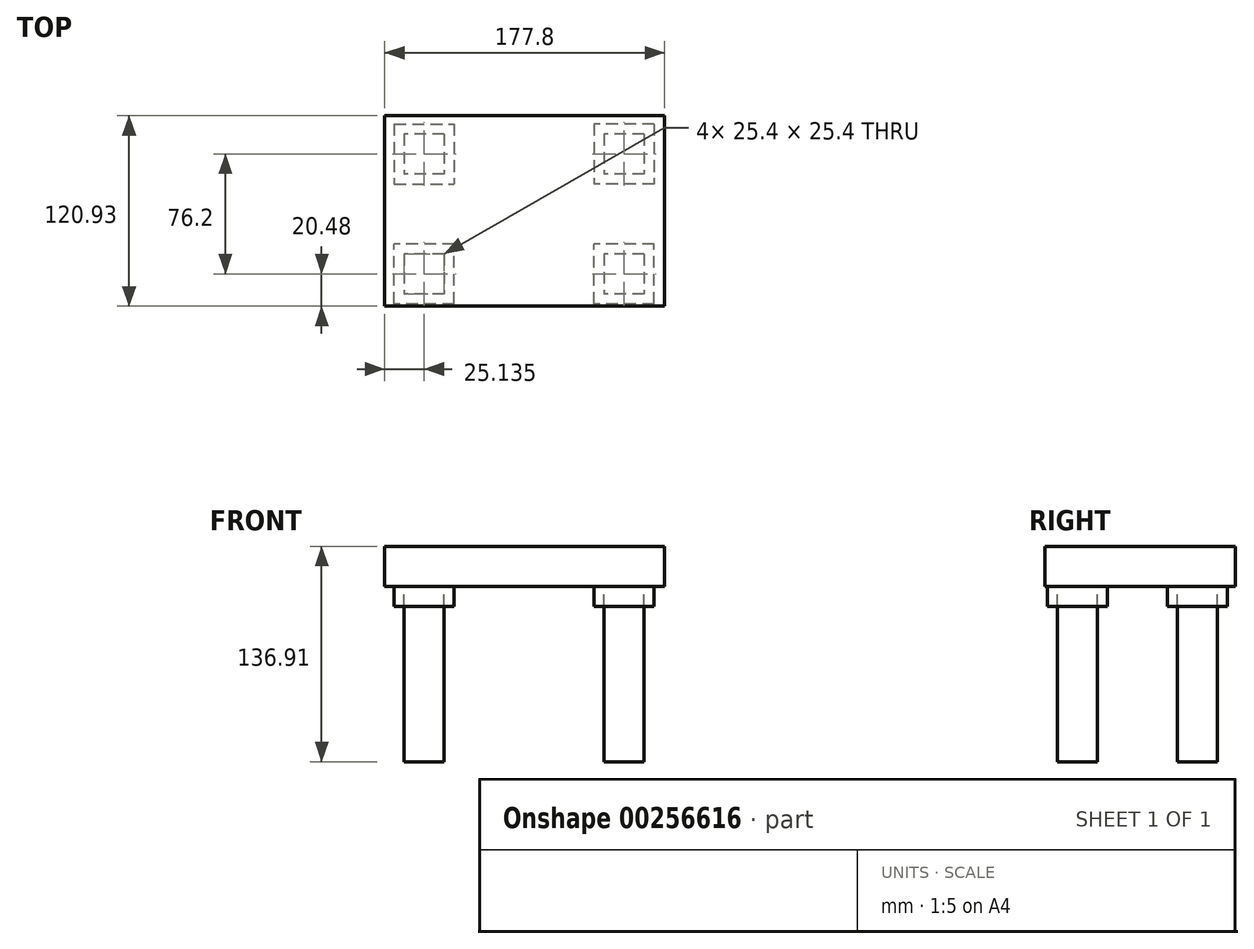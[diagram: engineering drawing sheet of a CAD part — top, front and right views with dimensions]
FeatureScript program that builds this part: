
annotation { "Feature Type Name" : "Feature", "Feature Type Description" : "" }
export const myFeature = defineFeature(function(context is Context, id is Id, definition is map)
    precondition{}
    {
        {
            var Q0;
            Q0=qCreatedBy(makeId("Top.planeOp"),FACE);
            var sketch = newSketch(context, id + "F0", { "sketchPlane" : qUnion([Q0])});
            skLineSegment(sketch, "E0.bottom", {"start": v(-24.92, 50.96) * mm, "end": v(-50.32, 50.96) * mm});
            skLineSegment(sketch, "E0.top", {"start": v(-24.92, 25.56) * mm, "end": v(-50.32, 25.56) * mm});
            skLineSegment(sketch, "E0.left", {"start": v(-24.92, 50.96) * mm, "end": v(-24.92, 25.56) * mm});
            skLineSegment(sketch, "E0.right", {"start": v(-50.32, 50.96) * mm, "end": v(-50.32, 25.56) * mm});
            skPoint(sketch, "E0.middle", {"position": v(-37.62, 38.26) * mm});
            skLineSegment(sketch, "E1", {"start": v(-37.62, 38.26) * mm, "end": v(89.38, 38.26) * mm});
            skLineSegment(sketch, "E2.bottom", {"start": v(102.08, 50.96) * mm, "end": v(76.68, 50.96) * mm});
            skLineSegment(sketch, "E2.top", {"start": v(102.08, 25.56) * mm, "end": v(76.68, 25.56) * mm});
            skLineSegment(sketch, "E2.left", {"start": v(102.08, 50.96) * mm, "end": v(102.08, 25.56) * mm});
            skLineSegment(sketch, "E2.right", {"start": v(76.68, 50.96) * mm, "end": v(76.68, 25.56) * mm});
            skPoint(sketch, "E2.middle", {"position": v(89.38, 38.26) * mm});
            skLineSegment(sketch, "E3", {"start": v(-37.62, 38.26) * mm, "end": v(-37.62, -37.94) * mm});
            skLineSegment(sketch, "E4.bottom", {"start": v(-24.92, -25.24) * mm, "end": v(-50.32, -25.24) * mm});
            skLineSegment(sketch, "E4.top", {"start": v(-24.92, -50.64) * mm, "end": v(-50.32, -50.64) * mm});
            skLineSegment(sketch, "E4.left", {"start": v(-24.92, -25.24) * mm, "end": v(-24.92, -50.64) * mm});
            skLineSegment(sketch, "E4.right", {"start": v(-50.32, -25.24) * mm, "end": v(-50.32, -50.64) * mm});
            skPoint(sketch, "E4.middle", {"position": v(-37.62, -37.94) * mm});
            skLineSegment(sketch, "E5", {"start": v(-37.62, -37.94) * mm, "end": v(89.38, -37.94) * mm});
            skLineSegment(sketch, "E6.bottom", {"start": v(102.08, -25.24) * mm, "end": v(76.68, -25.24) * mm});
            skLineSegment(sketch, "E6.top", {"start": v(102.08, -50.64) * mm, "end": v(76.68, -50.64) * mm});
            skLineSegment(sketch, "E6.left", {"start": v(102.08, -25.24) * mm, "end": v(102.08, -50.64) * mm});
            skLineSegment(sketch, "E6.right", {"start": v(76.68, -25.24) * mm, "end": v(76.68, -50.64) * mm});
            skPoint(sketch, "E6.middle", {"position": v(89.38, -37.94) * mm});
            skLineSegment(sketch, "E7", {"start": v(89.38, 38.26) * mm, "end": v(89.38, -37.94) * mm});
            skLineSegment(sketch, "E8.bottom", {"start": v(-18.57, -56.99) * mm, "end": v(-56.67, -56.99) * mm});
            skLineSegment(sketch, "E8.top", {"start": v(-18.57, -18.89) * mm, "end": v(-56.67, -18.89) * mm});
            skLineSegment(sketch, "E8.left", {"start": v(-18.57, -56.99) * mm, "end": v(-18.57, -18.89) * mm});
            skLineSegment(sketch, "E8.right", {"start": v(-56.67, -56.99) * mm, "end": v(-56.67, -18.89) * mm});
            skLineSegment(sketch, "E9.bottom", {"start": v(108.43, -56.99) * mm, "end": v(70.33, -56.99) * mm});
            skLineSegment(sketch, "E9.top", {"start": v(108.43, -18.89) * mm, "end": v(70.33, -18.89) * mm});
            skLineSegment(sketch, "E9.left", {"start": v(108.43, -56.99) * mm, "end": v(108.43, -18.89) * mm});
            skLineSegment(sketch, "E9.right", {"start": v(70.33, -56.99) * mm, "end": v(70.33, -18.89) * mm});
            skLineSegment(sketch, "E10.bottom", {"start": v(108.43, 57.31) * mm, "end": v(70.33, 57.31) * mm});
            skLineSegment(sketch, "E10.top", {"start": v(108.43, 19.21) * mm, "end": v(70.33, 19.21) * mm});
            skLineSegment(sketch, "E10.left", {"start": v(108.43, 57.31) * mm, "end": v(108.43, 19.21) * mm});
            skLineSegment(sketch, "E10.right", {"start": v(70.33, 57.31) * mm, "end": v(70.33, 19.21) * mm});
            skLineSegment(sketch, "E11.bottom", {"start": v(-56.67, 57.31) * mm, "end": v(-18.57, 57.31) * mm});
            skLineSegment(sketch, "E11.top", {"start": v(-56.67, 19.21) * mm, "end": v(-18.57, 19.21) * mm});
            skLineSegment(sketch, "E11.left", {"start": v(-56.67, 57.31) * mm, "end": v(-56.67, 19.21) * mm});
            skLineSegment(sketch, "E11.right", {"start": v(-18.57, 57.31) * mm, "end": v(-18.57, 19.21) * mm});
            skSolve(sketch);
        }
        {
            var Q0;
            {var subQ4=sQuery(id+"F0.wireOp",EDGE,"E2.bottom");Q0=makeQuery(id+"F0.imprint","IMPRINT",FACE,{"disambiguationData":[TD([[makeQuery(id+"F0.imprint","IMPRINT",EDGE,{"derivedFrom":subQ4}),1.0]])]});}
            var Q1;
            {var subQ1=sQuery(id+"F0.wireOp",EDGE,"E4.top");Q1=makeQuery(id+"F0.imprint","IMPRINT",FACE,{"disambiguationData":[TD([[makeQuery(id+"F0.imprint","IMPRINT",EDGE,{"derivedFrom":subQ1}),-1.0]])]});}
            var Q2;
            {var subQ1=sQuery(id+"F0.wireOp",EDGE,"E6.top");Q2=makeQuery(id+"F0.imprint","IMPRINT",FACE,{"disambiguationData":[TD([[makeQuery(id+"F0.imprint","IMPRINT",EDGE,{"derivedFrom":subQ1}),-1.0]])]});}
            var Q3;
            {var subQ0=sQuery(id+"F0.wireOp",EDGE,"E0.left");var subQ1=sQuery(id+"F0.wireOp",EDGE,"E0.top");var subQ2=makeQuery(id+"F0.imprint","INTERSECT",VERTEX,{"derivedFrom":[subQ1,subQ0]});Q3=makeQuery(id+"F0.imprint","IMPRINT",FACE,{"disambiguationData":[TD([[makeQuery(id+"F0.imprint","IMPRINT",EDGE,{"disambiguationData":[TD([[subQ2,-1.0]])],"derivedFrom":subQ1}),-1.0]])]});}
            var Q4;
            {var subQ0=sQuery(id+"F0.wireOp",EDGE,"E7");var subQ1=sQuery(id+"F0.wireOp",EDGE,"E1");var subQ2=makeQuery(id+"F0.imprint","INTERSECT",VERTEX,{"derivedFrom":[subQ1,subQ0]});Q4=makeQuery(id+"F0.imprint","IMPRINT",FACE,{"disambiguationData":[TD([[makeQuery(id+"F0.imprint","IMPRINT",EDGE,{"disambiguationData":[TD([[subQ2,1.0]])],"derivedFrom":subQ1}),-1.0]])]});}
            var Q5;
            {var subQ0=sQuery(id+"F0.wireOp",EDGE,"E5");var subQ1=sQuery(id+"F0.wireOp",EDGE,"E3");var subQ2=makeQuery(id+"F0.imprint","INTERSECT",VERTEX,{"derivedFrom":[subQ1,subQ0]});Q5=makeQuery(id+"F0.imprint","IMPRINT",FACE,{"disambiguationData":[TD([[makeQuery(id+"F0.imprint","IMPRINT",EDGE,{"disambiguationData":[TD([[subQ2,1.0]])],"derivedFrom":subQ1}),1.0]])]});}
            var Q6;
            {var subQ0=sQuery(id+"F0.wireOp",EDGE,"E7");var subQ1=sQuery(id+"F0.wireOp",EDGE,"E5");var subQ2=makeQuery(id+"F0.imprint","INTERSECT",VERTEX,{"derivedFrom":[subQ1,subQ0]});Q6=makeQuery(id+"F0.imprint","IMPRINT",FACE,{"disambiguationData":[TD([[makeQuery(id+"F0.imprint","IMPRINT",EDGE,{"disambiguationData":[TD([[subQ2,1.0]])],"derivedFrom":subQ1}),1.0]])]});}
            var Q7;
            {var subQ2=sQuery(id+"F0.wireOp",EDGE,"E0.bottom");Q7=makeQuery(id+"F0.imprint","IMPRINT",FACE,{"disambiguationData":[TD([[makeQuery(id+"F0.imprint","IMPRINT",EDGE,{"derivedFrom":subQ2}),1.0]])]});}
            extrude(context, id + "F1", {"entities" : qUnion([Q0, Q1, Q2, Q3, Q4, Q5, Q6, Q7]), "oppositeDirection" : true, "depth" : 111.5 * mm});
        }
        {
            var Q0;
            Q0=qCreatedBy(makeId("Top.planeOp"),FACE);
            var sketch = newSketch(context, id + "F2", { "sketchPlane" : qUnion([Q0])});
            skLineSegment(sketch, "E12.bottom", {"start": v(-62.75, 62.51) * mm, "end": v(115.05, 62.51) * mm});
            skLineSegment(sketch, "E12.top", {"start": v(-62.75, -58.42) * mm, "end": v(115.05, -58.42) * mm});
            skLineSegment(sketch, "E12.left", {"start": v(-62.75, 62.51) * mm, "end": v(-62.75, -58.42) * mm});
            skLineSegment(sketch, "E12.right", {"start": v(115.05, 62.51) * mm, "end": v(115.05, -58.42) * mm});
            skSolve(sketch);
        }
        {
            var Q0;
            Q0 = qSketchRegion(id + "F2", true);
            extrude(context, id + "F3", {"entities" : qUnion([Q0]), "depth" : 25.4 * mm});
        }
        {
            var Q0;
            {var subQ1=sQuery(id+"F0.wireOp",EDGE,"E4.top");Q0=makeQuery(id+"F0.imprint","IMPRINT",FACE,{"disambiguationData":[TD([[makeQuery(id+"F0.imprint","IMPRINT",EDGE,{"derivedFrom":subQ1}),1.0]])]});}
            var Q1;
            {var subQ7=sQuery(id+"F0.wireOp",EDGE,"E3");var subQ9=sQuery(id+"F0.wireOp",EDGE,"E8.top");var subQ11=makeQuery(id+"F0.imprint","INTERSECT",VERTEX,{"derivedFrom":[subQ7,subQ9]});Q1=makeQuery(id+"F0.imprint","IMPRINT",FACE,{"disambiguationData":[TD([[makeQuery(id+"F0.imprint","IMPRINT",EDGE,{"disambiguationData":[TD([[subQ11,-1.0]])],"derivedFrom":subQ7}),1.0]])]});}
            var Q2;
            {var subQ1=sQuery(id+"F0.wireOp",EDGE,"E6.top");Q2=makeQuery(id+"F0.imprint","IMPRINT",FACE,{"disambiguationData":[TD([[makeQuery(id+"F0.imprint","IMPRINT",EDGE,{"derivedFrom":subQ1}),1.0]])]});}
            var Q3;
            {var subQ7=sQuery(id+"F0.wireOp",EDGE,"E5");var subQ9=sQuery(id+"F0.wireOp",EDGE,"E9.right");var subQ10=makeQuery(id+"F0.imprint","INTERSECT",VERTEX,{"derivedFrom":[subQ7,subQ9]});Q3=makeQuery(id+"F0.imprint","IMPRINT",FACE,{"disambiguationData":[TD([[makeQuery(id+"F0.imprint","IMPRINT",EDGE,{"disambiguationData":[TD([[subQ10,-1.0]])],"derivedFrom":subQ7}),1.0]])]});}
            var Q4;
            {var subQ3=sQuery(id+"F0.wireOp",EDGE,"E1");var subQ5=sQuery(id+"F0.wireOp",EDGE,"E10.right");var subQ8=makeQuery(id+"F0.imprint","INTERSECT",VERTEX,{"derivedFrom":[subQ3,subQ5]});Q4=makeQuery(id+"F0.imprint","IMPRINT",FACE,{"disambiguationData":[TD([[makeQuery(id+"F0.imprint","IMPRINT",EDGE,{"disambiguationData":[TD([[subQ8,-1.0]])],"derivedFrom":subQ3}),-1.0]])]});}
            var Q5;
            {var subQ5=sQuery(id+"F0.wireOp",EDGE,"E2.bottom");Q5=makeQuery(id+"F0.imprint","IMPRINT",FACE,{"disambiguationData":[TD([[makeQuery(id+"F0.imprint","IMPRINT",EDGE,{"derivedFrom":subQ5}),-1.0]])]});}
            var Q6;
            {var subQ3=sQuery(id+"F0.wireOp",EDGE,"E0.left");var subQ8=sQuery(id+"F0.wireOp",EDGE,"E0.top");var subQ10=makeQuery(id+"F0.imprint","INTERSECT",VERTEX,{"derivedFrom":[subQ8,subQ3]});Q6=makeQuery(id+"F0.imprint","IMPRINT",FACE,{"disambiguationData":[TD([[makeQuery(id+"F0.imprint","IMPRINT",EDGE,{"disambiguationData":[TD([[subQ10,-1.0]])],"derivedFrom":subQ8}),1.0]])]});}
            var Q7;
            {var subQ2=sQuery(id+"F0.wireOp",EDGE,"E0.bottom");Q7=makeQuery(id+"F0.imprint","IMPRINT",FACE,{"disambiguationData":[TD([[makeQuery(id+"F0.imprint","IMPRINT",EDGE,{"derivedFrom":subQ2}),-1.0]])]});}
            extrude(context, id + "F4", {"entities" : qUnion([Q0, Q1, Q2, Q3, Q4, Q5, Q6, Q7]), "oppositeDirection" : true, "depth" : 12.7 * mm});
        }
    });
